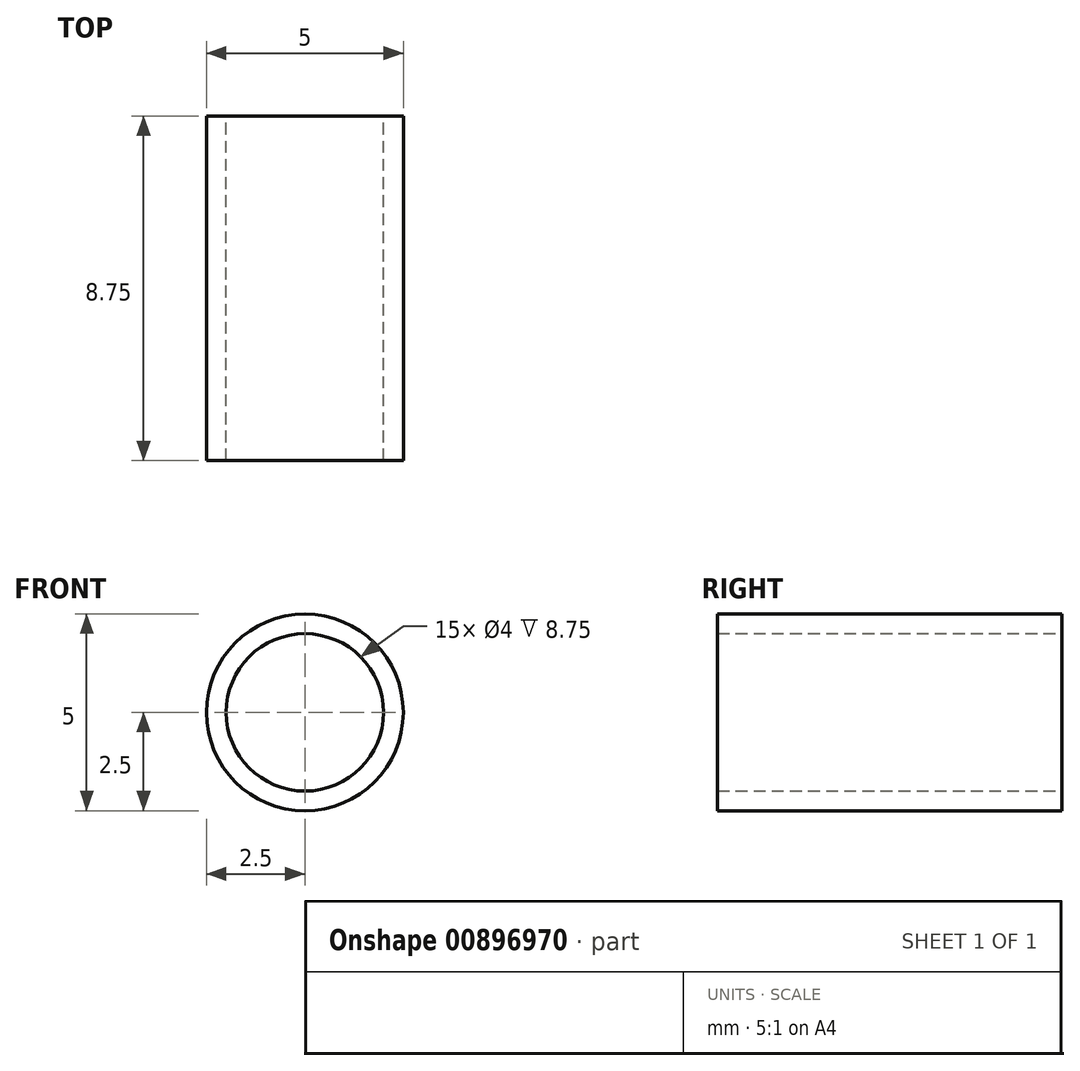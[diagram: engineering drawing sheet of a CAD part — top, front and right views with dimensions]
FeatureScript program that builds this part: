
annotation { "Feature Type Name" : "Feature", "Feature Type Description" : "" }
export const myFeature = defineFeature(function(context is Context, id is Id, definition is map)
    precondition{}
    {
        {
            var Q0;
            Q0=qCreatedBy(makeId("Front.planeOp"),FACE);
            var sketch = newSketch(context, id + "F0", { "sketchPlane" : qUnion([Q0])});
            skCircle(sketch, "E0", {"center": v(0, 0) * mm, "radius": 2.5 * mm});
            skCircle(sketch, "E1", {"center": v(0, 0) * mm, "radius": 2 * mm});
            skSolve(sketch);
        }
        {
            var Q0;
            Q0=qSketchRegion(id+"F0",true);
            extrude(context, id + "F1", {"entities" : qUnion([Q0]), "depth" : 17.5 * mm / 2});
        }
    });
